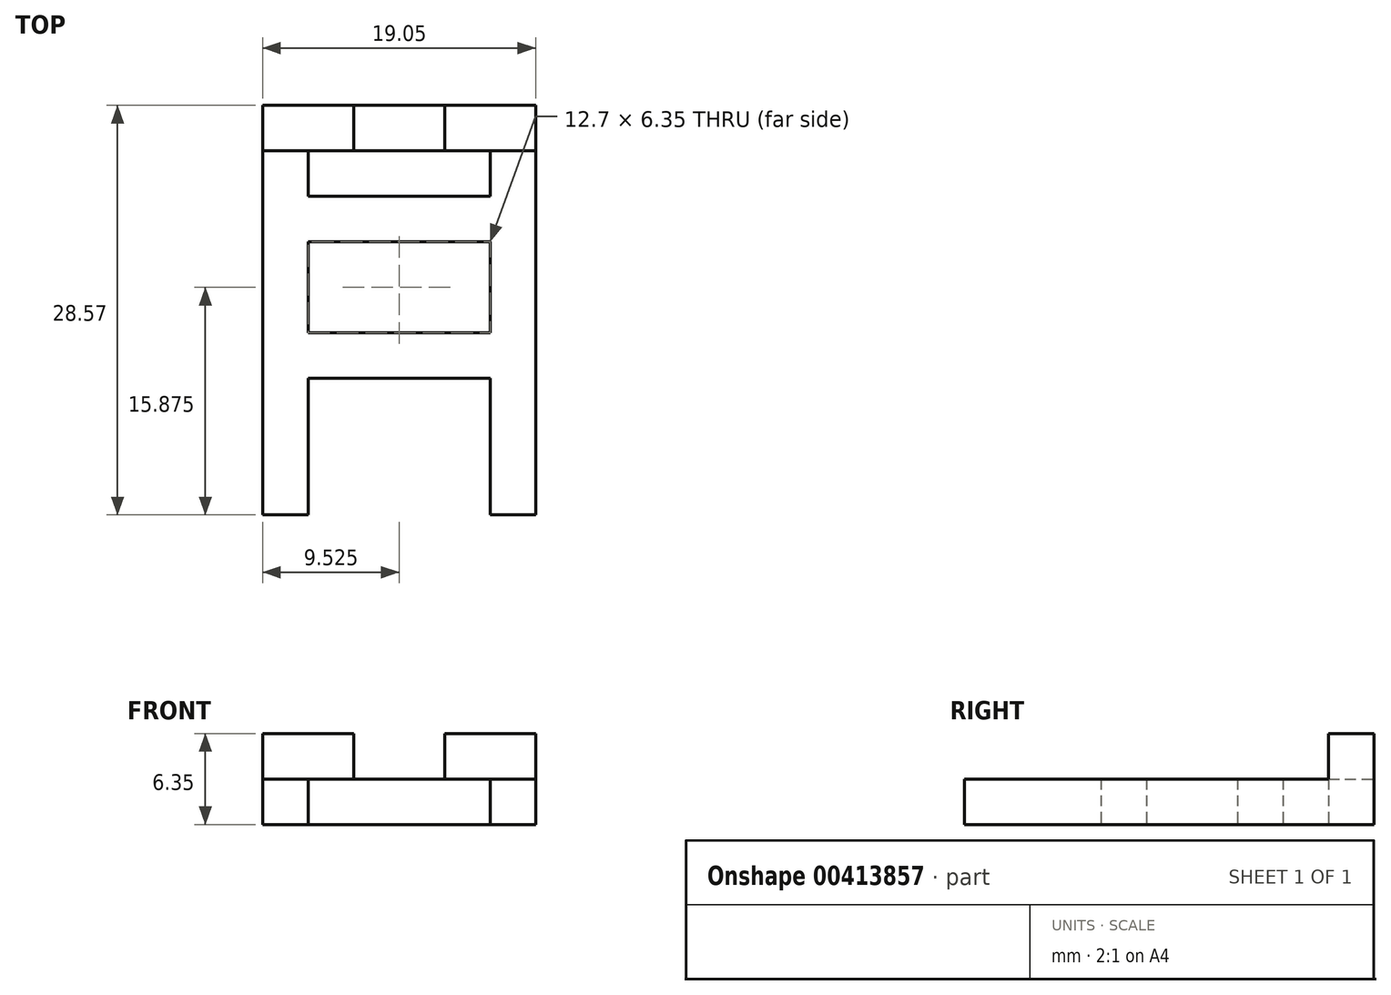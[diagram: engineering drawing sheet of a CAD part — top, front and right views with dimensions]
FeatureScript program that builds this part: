
annotation { "Feature Type Name" : "Feature", "Feature Type Description" : "" }
export const myFeature = defineFeature(function(context is Context, id is Id, definition is map)
    precondition{}
    {
        {
            var Q0;
            Q0=qCreatedBy(makeId("Top.planeOp"),FACE);
            var sketch = newSketch(context, id + "F0", { "sketchPlane" : qUnion([Q0])});
            skLineSegment(sketch, "E0", {"start": v(0, 0) * mm, "end": v(0, 25.4) * mm});
            skLineSegment(sketch, "E1", {"start": v(0, 0) * mm, "end": v(3.18, 0) * mm});
            skLineSegment(sketch, "E2", {"start": v(19.05, 0) * mm, "end": v(19.05, 25.4) * mm});
            skLineSegment(sketch, "E3.0", {"start": v(0, 3.18) * mm, "end": v(3.18, 3.18) * mm});
            skLineSegment(sketch, "E4.0", {"start": v(3.18, 0) * mm, "end": v(3.18, 25.4) * mm});
            skLineSegment(sketch, "E5.0", {"start": v(15.88, 0) * mm, "end": v(15.87, 25.4) * mm});
            skLineSegment(sketch, "E6", {"start": v(0, 25.4) * mm, "end": v(3.18, 25.4) * mm});
            skLineSegment(sketch, "E7", {"start": v(15.87, 25.4) * mm, "end": v(19.05, 25.4) * mm});
            skLineSegment(sketch, "E8.0", {"start": v(0, 9.53) * mm, "end": v(19.05, 9.53) * mm});
            skLineSegment(sketch, "E9.0", {"start": v(0, 12.7) * mm, "end": v(19.05, 12.7) * mm});
            skLineSegment(sketch, "E10.0", {"start": v(0, 19.05) * mm, "end": v(19.05, 19.05) * mm});
            skLineSegment(sketch, "E11.0", {"start": v(0, 22.23) * mm, "end": v(19.05, 22.23) * mm});
            skLineSegment(sketch, "E12.trimOffspring", {"start": v(15.88, 0) * mm, "end": v(19.05, 0) * mm});
            skLineSegment(sketch, "E13.trimOffspring", {"start": v(15.88, 3.18) * mm, "end": v(19.05, 3.18) * mm});
            skSolve(sketch);
        }
        {
            var Q0;
            Q0 = qSketchRegion(id + "F0", true);
            var Q1;
            {var subQ0=sQuery(id+"F0.wireOp",EDGE,"E8.0");var subQ1=sQuery(id+"F0.wireOp",EDGE,"E4.0");var subQ2=makeQuery(id+"F0.imprint","INTERSECT",VERTEX,{"derivedFrom":[subQ1,subQ0]});Q1=makeQuery(id+"F0.imprint","IMPRINT",FACE,{"disambiguationData":[TD([[makeQuery(id+"F0.imprint","IMPRINT",EDGE,{"disambiguationData":[TD([[subQ2,-1.0]])],"derivedFrom":subQ1}),-1.0]])]});}
            extrude(context, id + "F1", {"entities" : qUnion([Q0, Q1]), "depth" : 3.17 * mm});
        }
        {
            var Q0;
            Q0=makeQuery(id+"F1.opExtrude","CAP_FACE",FACE,{"disambiguationData":[OSD([sQuery(id+"F0.wireOp",EDGE,"E0"),sQuery(id+"F0.wireOp",EDGE,"E1"),sQuery(id+"F0.wireOp",EDGE,"E2"),sQuery(id+"F0.wireOp",EDGE,"E3.0"),sQuery(id+"F0.wireOp",EDGE,"E4.0"),sQuery(id+"F0.wireOp",EDGE,"E5.0"),sQuery(id+"F0.wireOp",EDGE,"E6"),sQuery(id+"F0.wireOp",EDGE,"E7"),sQuery(id+"F0.wireOp",EDGE,"E8.0"),sQuery(id+"F0.wireOp",EDGE,"E9.0"),sQuery(id+"F0.wireOp",EDGE,"E10.0"),sQuery(id+"F0.wireOp",EDGE,"E11.0")])],"isStart":true});
            var sketch = newSketch(context, id + "F2", { "sketchPlane" : qUnion([Q0])});
            skLineSegment(sketch, "E14", {"start": v(19.05, -25.4) * mm, "end": v(0, -25.4) * mm});
            skLineSegment(sketch, "E15", {"start": v(0, -25.4) * mm, "end": v(0, -28.58) * mm});
            skLineSegment(sketch, "E16", {"start": v(0, -28.58) * mm, "end": v(19.05, -28.58) * mm});
            skLineSegment(sketch, "E17", {"start": v(19.05, -28.58) * mm, "end": v(19.05, -25.4) * mm});
            skSolve(sketch);
        }
        {
            var Q0;
            Q0 = qSketchRegion(id + "F2", true);
            extrude(context, id + "F3", {"entities" : qUnion([Q0]), "operationType" : NewBodyOperationType.ADD, "oppositeDirection" : true, "depth" : 6.35 * mm});
        }
        {
            var Q0;
            Q0=makeQuery(id+"F3.opExtrude","SWEPT_FACE",FACE,{"disambiguationData":[OSD([sQuery(id+"F2.wireOp",EDGE,"E16")])]});
            var sketch = newSketch(context, id + "F4", { "sketchPlane" : qUnion([Q0])});
            skLineSegment(sketch, "E18", {"start": v(0, 6.35) * mm, "end": v(-6.35, 6.35) * mm});
            skLineSegment(sketch, "E19", {"start": v(-6.35, 6.35) * mm, "end": v(-6.35, 3.18) * mm});
            skLineSegment(sketch, "E20", {"start": v(-6.35, 3.18) * mm, "end": v(-12.7, 3.18) * mm});
            skPoint(sketch, "E20.endSnap0", {"position": v(-19.05, 3.18) * mm});
            skLineSegment(sketch, "E21", {"start": v(-12.7, 3.18) * mm, "end": v(-12.7, 6.35) * mm});
            skLineSegment(sketch, "E22", {"start": v(-12.7, 6.35) * mm, "end": v(-6.35, 6.35) * mm});
            skSolve(sketch);
        }
        {
            var Q0;
            Q0 = qSketchRegion(id + "F4", true);
            extrude(context, id + "F5", {"entities" : qUnion([Q0]), "operationType" : NewBodyOperationType.REMOVE, "oppositeDirection" : true, "depth" : 25.4 * mm});
        }
    });
